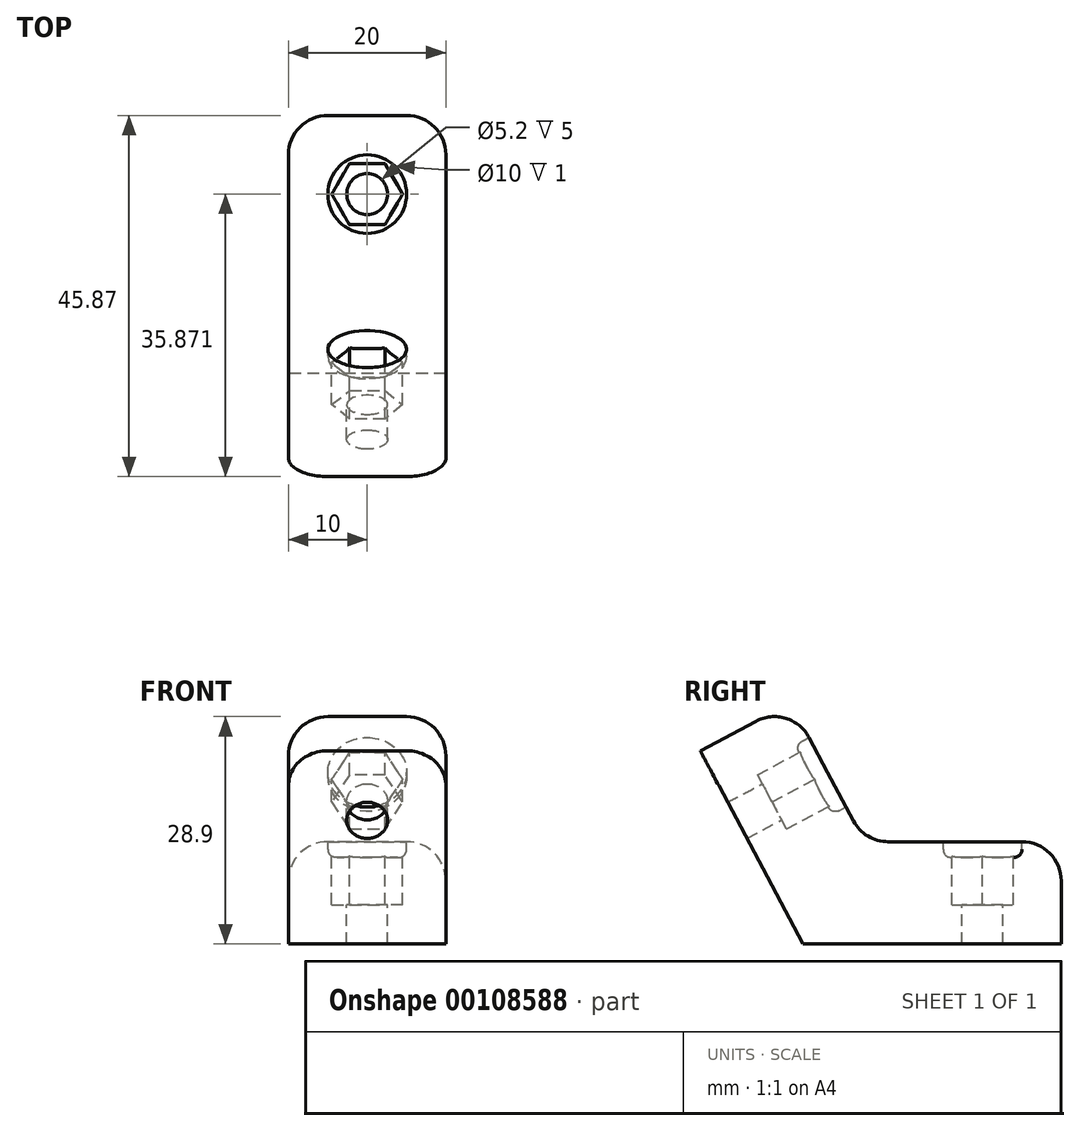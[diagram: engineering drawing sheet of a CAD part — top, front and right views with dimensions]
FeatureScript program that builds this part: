
annotation { "Feature Type Name" : "Feature", "Feature Type Description" : "" }
export const myFeature = defineFeature(function(context is Context, id is Id, definition is map)
    precondition{}
    {
        {
            assignVariable(context, id + "F0", {"name" : "Pladetykkelse", "anyValue" : 9});
        }
        {
            assignVariable(context, id + "F1", {"name" : "boltlength", "anyValue" : 20});
        }
        {
            assignVariable(context, id + "F2", {"name" : "Tykkelse", "anyValue" : (getVariable(context, 'boltlength') - getVariable(context, 'Pladetykkelse') + 2)});
        }
        {
            var Q0;
            Q0=qCreatedBy(makeId("Right.planeOp"),FACE);
            var sketch = newSketch(context, id + "F3", { "sketchPlane" : qUnion([Q0])});
            skLineSegment(sketch, "E0.bottom", {"start": v(0, 0) * mm, "end": v(32.81, 0) * mm});
            skLineSegment(sketch, "E0.top", {"start": v(7.81, 13) * mm, "end": v(32.81, 13) * mm});
            skLineSegment(sketch, "E0.right", {"start": v(32.81, 0) * mm, "end": v(32.81, 13) * mm});
            skLineSegment(sketch, "E1", {"start": v(0, 0) * mm, "end": v(-13.06, 24.56) * mm});
            skLineSegment(sketch, "E2", {"start": v(-13.06, 24.56) * mm, "end": v(-1.58, 30.66) * mm});
            skLineSegment(sketch, "E3", {"start": v(-1.58, 30.66) * mm, "end": v(7.81, 13) * mm});
            skLineSegment(sketch, "E4", {"start": v(7.81, 13) * mm, "end": v(-3.67, 6.9) * mm, "construction": true});
            skLineSegment(sketch, "E5", {"start": v(7.81, 13) * mm, "end": v(-6.91, 13) * mm, "construction": true});
            skLineSegment(sketch, "E6", {"start": v(-6.91, 13) * mm, "end": v(4.57, 19.1) * mm, "construction": true});
            skSolve(sketch);
        }
        {
            var Q0;
            Q0=makeQuery(id+"F3.imprint","IMPRINT",FACE,{"disambiguationData":[TD([[makeQuery(id+"F3.imprint","IMPRINT",EDGE,{"derivedFrom":sQuery(id+"F3.wireOp",EDGE,"E0.bottom")}),1.0]])]});
            extrude(context, id + "F4", {"entities" : qUnion([Q0]), "depth" : 20 * mm});
        }
        {
            var Q0;
            Q0=makeQuery(id+"F4.opExtrude","SWEPT_FACE",FACE,{"disambiguationData":[OSD([sQuery(id+"F3.wireOp",EDGE,"E3")])]});
            var sketch = newSketch(context, id + "F5", { "sketchPlane" : qUnion([Q0])});
            skLineSegment(sketch, "E7.0", {"start": v(-20, 27.81) * mm, "end": v(0, 27.81) * mm, "construction": true});
            skLineSegment(sketch, "E8.0", {"start": v(-20, 27.81) * mm, "end": v(-20, 7.81) * mm, "construction": true});
            skLineSegment(sketch, "E9.0", {"start": v(0, 27.81) * mm, "end": v(0, 7.81) * mm, "construction": true});
            skLineSegment(sketch, "E10.0", {"start": v(-20, 7.81) * mm, "end": v(0, 7.81) * mm, "construction": true});
            skLineSegment(sketch, "E11", {"start": v(-10, 27.81) * mm, "end": v(-10, 7.81) * mm, "construction": true});
            skCircle(sketch, "E12", {"center": v(-10, 17.81) * mm, "radius": 2.6 * mm});
            skCircle(sketch, "E13.cCircle", {"center": v(-10, 17.81) * mm, "radius": 4.5 * mm, "construction": true});
            skLineSegment(sketch, "E13.0", {"start": v(-12.25, 21.7) * mm, "end": v(-7.75, 21.7) * mm});
            skLineSegment(sketch, "E13.1", {"start": v(-7.75, 21.7) * mm, "end": v(-5.5, 17.81) * mm});
            skLineSegment(sketch, "E13.2", {"start": v(-5.5, 17.81) * mm, "end": v(-7.75, 13.91) * mm});
            skLineSegment(sketch, "E13.3", {"start": v(-7.75, 13.91) * mm, "end": v(-12.25, 13.91) * mm});
            skLineSegment(sketch, "E13.4", {"start": v(-12.25, 13.91) * mm, "end": v(-14.5, 17.81) * mm});
            skLineSegment(sketch, "E13.5", {"start": v(-14.5, 17.81) * mm, "end": v(-12.25, 21.7) * mm});
            skCircle(sketch, "E14", {"center": v(-10, 17.81) * mm, "radius": 5 * mm});
            skSolve(sketch);
        }
        {
            var Q0;
            Q0=makeQuery(id+"F5.imprint","IMPRINT",FACE,{"disambiguationData":[TD([[makeQuery(id+"F5.imprint","IMPRINT",EDGE,{"derivedFrom":sQuery(id+"F5.wireOp",EDGE,"E12")}),1.0]])]});
            extrude(context, id + "F6", {"entities" : qUnion([Q0]), "operationType" : NewBodyOperationType.REMOVE, "endBound" : BoundingType.THROUGH_ALL, "oppositeDirection" : true, "depth" : 25 * mm});
        }
        {
            var Q0;
            Q0=makeQuery(id+"F5.imprint","IMPRINT",FACE,{"disambiguationData":[TD([[makeQuery(id+"F5.imprint","IMPRINT",EDGE,{"derivedFrom":sQuery(id+"F5.wireOp",EDGE,"E12")}),-1.0]])]});
            extrude(context, id + "F7", {"entities" : qUnion([Q0]), "operationType" : NewBodyOperationType.REMOVE, "oppositeDirection" : true, "depth" : (getVariable(context, 'Tykkelse') - (getVariable(context, 'boltlength') - getVariable(context, 'Pladetykkelse')) + 6) * mm});
        }
        {
            var Q0;
            Q0=makeQuery(id+"F5.imprint","IMPRINT",FACE,{"disambiguationData":[TD([[makeQuery(id+"F5.imprint","IMPRINT",EDGE,{"derivedFrom":sQuery(id+"F5.wireOp",EDGE,"E13.0")}),1.0]])]});
            var Q1;
            Q1=sQuery(id+"F5.wireOp",EDGE,"E14");
            extrude(context, id + "F8", {"entities" : qUnion([Q0]), "operationType" : NewBodyOperationType.REMOVE, "surfaceEntities" : qUnion([Q1]), "oppositeDirection" : true, "depth" : (getVariable(context, 'Tykkelse') - (getVariable(context, 'boltlength') - getVariable(context, 'Pladetykkelse'))) * mm});
        }
        {
            var Q0;
            Q0=makeQuery(id+"F4.opExtrude","SWEPT_FACE",FACE,{"disambiguationData":[OSD([sQuery(id+"F3.wireOp",EDGE,"E0.top")])]});
            var sketch = newSketch(context, id + "F9", { "sketchPlane" : qUnion([Q0])});
            skLineSegment(sketch, "E15.0", {"start": v(0, 32.81) * mm, "end": v(20, 32.81) * mm, "construction": true});
            skLineSegment(sketch, "E16.0", {"start": v(0, 32.81) * mm, "end": v(0, 7.81) * mm, "construction": true});
            skLineSegment(sketch, "E17.0", {"start": v(20, 32.81) * mm, "end": v(20, 7.81) * mm, "construction": true});
            skLineSegment(sketch, "E18.0", {"start": v(0, 7.81) * mm, "end": v(20, 7.81) * mm, "construction": true});
            skLineSegment(sketch, "E19", {"start": v(10, 32.81) * mm, "end": v(10, 7.81) * mm, "construction": true});
            skCircle(sketch, "E20", {"center": v(10, 22.81) * mm, "radius": 2.6 * mm});
            skCircle(sketch, "E21.cCircle", {"center": v(10, 22.81) * mm, "radius": 4.5 * mm, "construction": true});
            skLineSegment(sketch, "E21.0", {"start": v(7.75, 26.7) * mm, "end": v(12.25, 26.7) * mm});
            skLineSegment(sketch, "E21.1", {"start": v(12.25, 26.7) * mm, "end": v(14.5, 22.81) * mm});
            skLineSegment(sketch, "E21.2", {"start": v(14.5, 22.81) * mm, "end": v(12.25, 18.91) * mm});
            skLineSegment(sketch, "E21.3", {"start": v(12.25, 18.91) * mm, "end": v(7.75, 18.91) * mm});
            skLineSegment(sketch, "E21.4", {"start": v(7.75, 18.91) * mm, "end": v(5.5, 22.81) * mm});
            skLineSegment(sketch, "E21.5", {"start": v(5.5, 22.81) * mm, "end": v(7.75, 26.7) * mm});
            skCircle(sketch, "E22", {"center": v(10, 22.81) * mm, "radius": 5 * mm});
            skSolve(sketch);
        }
        {
            var Q0;
            Q0=makeQuery(id+"F9.imprint","IMPRINT",FACE,{"disambiguationData":[TD([[makeQuery(id+"F9.imprint","IMPRINT",EDGE,{"derivedFrom":sQuery(id+"F9.wireOp",EDGE,"E20")}),1.0]])]});
            extrude(context, id + "F10", {"entities" : qUnion([Q0]), "operationType" : NewBodyOperationType.REMOVE, "endBound" : BoundingType.THROUGH_ALL, "oppositeDirection" : true, "depth" : 25 * mm});
        }
        {
            var Q0;
            Q0=makeQuery(id+"F9.imprint","IMPRINT",FACE,{"disambiguationData":[TD([[makeQuery(id+"F9.imprint","IMPRINT",EDGE,{"derivedFrom":sQuery(id+"F9.wireOp",EDGE,"E20")}),-1.0]])]});
            extrude(context, id + "F11", {"entities" : qUnion([Q0]), "operationType" : NewBodyOperationType.REMOVE, "oppositeDirection" : true, "depth" : (getVariable(context, 'Tykkelse') - (getVariable(context, 'boltlength') - getVariable(context, 'Pladetykkelse')) + 6) * mm});
        }
        {
            var Q0;
            Q0=makeQuery(id+"F9.imprint","IMPRINT",FACE,{"disambiguationData":[TD([[makeQuery(id+"F9.imprint","IMPRINT",EDGE,{"derivedFrom":sQuery(id+"F9.wireOp",EDGE,"E21.0")}),1.0]])]});
            var Q1;
            Q1=sQuery(id+"F9.wireOp",EDGE,"E22");
            extrude(context, id + "F12", {"entities" : qUnion([Q0]), "operationType" : NewBodyOperationType.REMOVE, "surfaceEntities" : qUnion([Q1]), "oppositeDirection" : true, "depth" : (getVariable(context, 'Tykkelse') - (getVariable(context, 'boltlength') - getVariable(context, 'Pladetykkelse'))) * mm});
        }
        {
            var Q0;
            Q0=makeQuery(id+"F8.boolean.opBoolean","COPY",EDGE,{"derivedFrom":makeQuery(id+"F8.opExtrude","CAP_EDGE",EDGE,{"disambiguationData":[OSD([sQuery(id+"F5.wireOp",EDGE,"E14")])],"isStart":false})});
            var Q1;
            Q1=makeQuery(id+"F12.boolean.opBoolean","COPY",EDGE,{"derivedFrom":makeQuery(id+"F12.opExtrude","CAP_EDGE",EDGE,{"disambiguationData":[OSD([sQuery(id+"F9.wireOp",EDGE,"E22")])],"isStart":false})});
            fillet(context, id + "F13", {"entities" : qUnion([Q0, Q1]), "radius" : 1 * mm, "tangentPropagation" : true, "allowEdgeOverflow" : false});
        }
        {
            var Q0;
            Q0=makeQuery(id+"F4.opExtrude","SWEPT_EDGE",EDGE,{"disambiguationData":[OSD([sQuery(id+"F3.wireOp",EDGE,"E0.top"),sQuery(id+"F3.wireOp",EDGE,"E3")])]});
            fillet(context, id + "F14", {"entities" : qUnion([Q0]), "radius" : 5 * mm, "tangentPropagation" : true, "allowEdgeOverflow" : false});
        }
        {
            var Q0;
            Q0=makeQuery(id+"F4.opExtrude","CAP_EDGE",EDGE,{"disambiguationData":[OSD([sQuery(id+"F3.wireOp",EDGE,"E2")])],"isStart":false});
            var Q1;
            Q1=makeQuery(id+"F4.opExtrude","CAP_EDGE",EDGE,{"disambiguationData":[OSD([sQuery(id+"F3.wireOp",EDGE,"E3")])],"isStart":false});
            var Q2;
            Q2=makeQuery(id+"F4.opExtrude","CAP_EDGE",EDGE,{"disambiguationData":[OSD([sQuery(id+"F3.wireOp",EDGE,"E0.right")])],"isStart":false});
            var Q3;
            Q3=makeQuery(id+"F4.opExtrude","CAP_EDGE",EDGE,{"disambiguationData":[OSD([sQuery(id+"F3.wireOp",EDGE,"E0.right")])],"isStart":true});
            var Q4;
            Q4=makeQuery(id+"F4.opExtrude","CAP_EDGE",EDGE,{"disambiguationData":[OSD([sQuery(id+"F3.wireOp",EDGE,"E0.top")])],"isStart":true});
            var Q5;
            Q5=makeQuery(id+"F4.opExtrude","CAP_EDGE",EDGE,{"disambiguationData":[OSD([sQuery(id+"F3.wireOp",EDGE,"E2")])],"isStart":true});
            var Q6;
            Q6=makeQuery(id+"F4.opExtrude","SWEPT_EDGE",EDGE,{"disambiguationData":[OSD([sQuery(id+"F3.wireOp",EDGE,"E0.top"),sQuery(id+"F3.wireOp",EDGE,"E0.right")])]});
            var Q7;
            Q7=makeQuery(id+"F4.opExtrude","SWEPT_EDGE",EDGE,{"disambiguationData":[OSD([sQuery(id+"F3.wireOp",EDGE,"E2"),sQuery(id+"F3.wireOp",EDGE,"E3")])]});
            fillet(context, id + "F15", {"entities" : qUnion([Q0, Q1, Q2, Q3, Q4, Q5, Q6, Q7]), "radius" : 5 * mm, "tangentPropagation" : true, "allowEdgeOverflow" : false});
        }
    });
